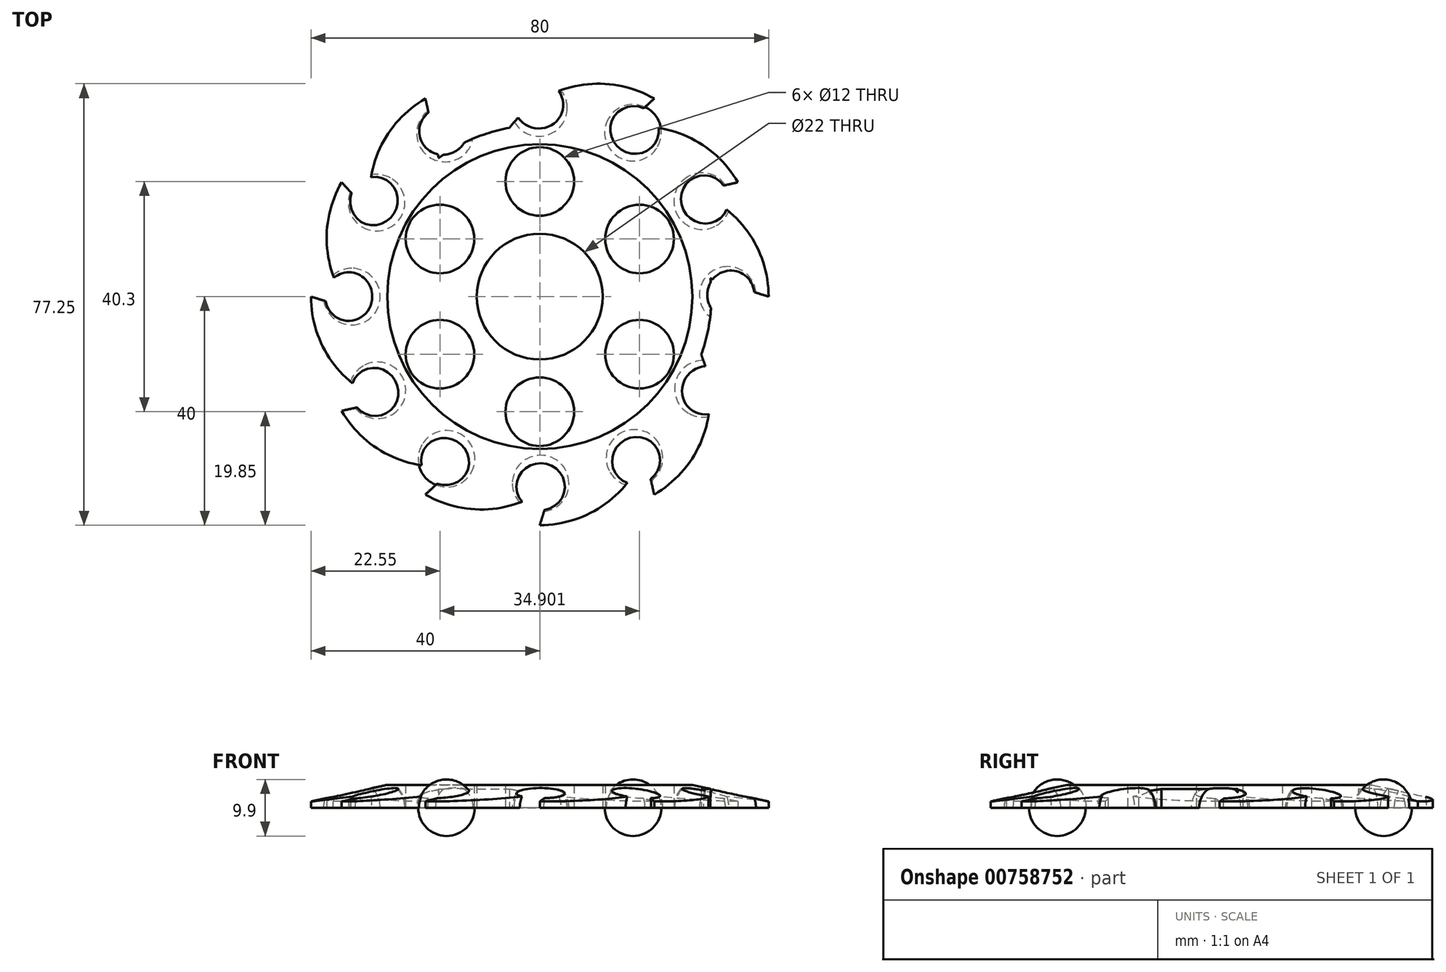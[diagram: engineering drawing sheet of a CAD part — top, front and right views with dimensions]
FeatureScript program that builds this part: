
annotation { "Feature Type Name" : "Feature", "Feature Type Description" : "" }
export const myFeature = defineFeature(function(context is Context, id is Id, definition is map)
    precondition{}
    {
        {
            assignVariable(context, id + "F0", {"name" : "thickness", "anyValue" : 8});
        }
        {
            var Q0;
            Q0=qCreatedBy(makeId("Top.planeOp"),FACE);
            var sketch = newSketch(context, id + "F1", { "sketchPlane" : qUnion([Q0])});
            skCircle(sketch, "E0", {"center": v(0, 0) * mm, "radius": 11 * mm});
            skCircle(sketch, "E1", {"center": v(0, 0) * mm, "radius": 40 * mm, "construction": true});
            skCircle(sketch, "E2", {"center": v(0, 0) * mm, "radius": 30 * mm});
            skLineSegment(sketch, "E3", {"start": v(-30, 0) * mm, "end": v(-11, 0) * mm, "construction": true});
            skPoint(sketch, "E4", {"position": v(-20.5, 0) * mm});
            skArc(sketch, "E5", {"start": v(-40, 0) * mm, "mid": v(-35.12, -12.9) * mm, "end": v(-22.93, -19.35) * mm});
            skArc(sketch, "E6.1.0", {"start": v(20, -34.64) * mm, "mid": v(28.73, -23.97) * mm, "end": v(28.22, -10.18) * mm});
            skArc(sketch, "E6.2.0", {"start": v(20, 34.64) * mm, "mid": v(6.39, 36.87) * mm, "end": v(-5.3, 29.53) * mm});
            skLineSegment(sketch, "E7", {"start": v(-40, 0) * mm, "end": v(-29.83, -3.17) * mm});
            skLineSegment(sketch, "E8.1.0", {"start": v(-34.64, -20) * mm, "end": v(-24.25, -17.66) * mm});
            skArc(sketch, "E8.1.1", {"start": v(-34.64, -20) * mm, "mid": v(-23.97, -28.73) * mm, "end": v(-10.18, -28.22) * mm});
            skLineSegment(sketch, "E8.2.0", {"start": v(-20, -34.64) * mm, "end": v(-12.17, -27.42) * mm});
            skArc(sketch, "E8.2.1", {"start": v(-20, -34.64) * mm, "mid": v(-6.39, -36.87) * mm, "end": v(5.3, -29.53) * mm});
            skLineSegment(sketch, "E9.1.3.0", {"start": v(0, -40) * mm, "end": v(3.17, -29.83) * mm});
            skArc(sketch, "E9.3.3.0", {"start": v(0, -40) * mm, "mid": v(12.9, -35.12) * mm, "end": v(19.35, -22.93) * mm});
            skLineSegment(sketch, "E9.1.4.0", {"start": v(20, -34.64) * mm, "end": v(17.66, -24.25) * mm});
            skLineSegment(sketch, "E9.1.5.0", {"start": v(34.64, -20) * mm, "end": v(27.42, -12.17) * mm});
            skArc(sketch, "E9.3.5.0", {"start": v(34.64, -20) * mm, "mid": v(36.87, -6.39) * mm, "end": v(29.53, 5.3) * mm});
            skLineSegment(sketch, "E10.1.6.0", {"start": v(40, 0) * mm, "end": v(29.83, 3.17) * mm});
            skArc(sketch, "E10.3.6.0", {"start": v(40, 0) * mm, "mid": v(35.12, 12.9) * mm, "end": v(22.93, 19.35) * mm});
            skLineSegment(sketch, "E10.1.7.0", {"start": v(34.64, 20) * mm, "end": v(24.25, 17.66) * mm});
            skArc(sketch, "E10.3.7.0", {"start": v(34.64, 20) * mm, "mid": v(23.97, 28.73) * mm, "end": v(10.18, 28.22) * mm});
            skLineSegment(sketch, "E11.1.8.0", {"start": v(20, 34.64) * mm, "end": v(12.17, 27.42) * mm});
            skLineSegment(sketch, "E11.1.9.0", {"start": v(0, 40) * mm, "end": v(-3.17, 29.83) * mm});
            skArc(sketch, "E11.3.9.0", {"start": v(0, 40) * mm, "mid": v(-12.9, 35.12) * mm, "end": v(-19.35, 22.93) * mm});
            skLineSegment(sketch, "E12.1.10.0", {"start": v(-20, 34.64) * mm, "end": v(-17.66, 24.25) * mm});
            skArc(sketch, "E12.3.10.0", {"start": v(-20, 34.64) * mm, "mid": v(-28.73, 23.97) * mm, "end": v(-28.22, 10.18) * mm});
            skLineSegment(sketch, "E12.1.11.0", {"start": v(-34.64, 20) * mm, "end": v(-27.42, 12.17) * mm});
            skArc(sketch, "E12.3.11.0", {"start": v(-34.64, 20) * mm, "mid": v(-36.87, 6.39) * mm, "end": v(-29.53, -5.3) * mm});
            skSolve(sketch);
        }
        {
            var Q0;
            {var subQ5=sQuery(id+"F1.wireOp",EDGE,"E8.2.1");var subQ7=sQuery(id+"F1.wireOp",EDGE,"E2");var subQ8=makeQuery(id+"F1.imprint","INTERSECT",VERTEX,{"derivedFrom":[subQ7,subQ5]});Q0=makeQuery(id+"F1.imprint","IMPRINT",FACE,{"disambiguationData":[TD([[makeQuery(id+"F1.imprint","IMPRINT",EDGE,{"disambiguationData":[TD([[subQ8,-1.0]])],"derivedFrom":subQ7}),-1.0]])]});}
            var Q1;
            {var subQ5=sQuery(id+"F1.wireOp",EDGE,"E9.3.3.0");var subQ7=sQuery(id+"F1.wireOp",EDGE,"E2");var subQ8=makeQuery(id+"F1.imprint","INTERSECT",VERTEX,{"derivedFrom":[subQ7,subQ5]});Q1=makeQuery(id+"F1.imprint","IMPRINT",FACE,{"disambiguationData":[TD([[makeQuery(id+"F1.imprint","IMPRINT",EDGE,{"disambiguationData":[TD([[subQ8,-1.0]])],"derivedFrom":subQ7}),-1.0]])]});}
            var Q2;
            {var subQ0=sQuery(id+"F1.wireOp",EDGE,"E8.2.1");var subQ1=sQuery(id+"F1.wireOp",EDGE,"E2");var subQ2=makeQuery(id+"F1.imprint","INTERSECT",VERTEX,{"derivedFrom":[subQ1,subQ0]});Q2=makeQuery(id+"F1.imprint","IMPRINT",FACE,{"disambiguationData":[TD([[makeQuery(id+"F1.imprint","IMPRINT",EDGE,{"disambiguationData":[TD([[subQ2,1.0]])],"derivedFrom":subQ1}),-1.0]])]});}
            var Q3;
            {var subQ3=sQuery(id+"F1.wireOp",EDGE,"E6.2.0");var subQ5=sQuery(id+"F1.wireOp",EDGE,"E2");var subQ6=makeQuery(id+"F1.imprint","INTERSECT",VERTEX,{"derivedFrom":[subQ5,subQ3]});Q3=makeQuery(id+"F1.imprint","IMPRINT",FACE,{"disambiguationData":[TD([[makeQuery(id+"F1.imprint","IMPRINT",EDGE,{"disambiguationData":[TD([[subQ6,-1.0]])],"derivedFrom":subQ5}),-1.0]])]});}
            var Q4;
            {var subQ5=sQuery(id+"F1.wireOp",EDGE,"E10.3.7.0");var subQ7=sQuery(id+"F1.wireOp",EDGE,"E2");var subQ8=makeQuery(id+"F1.imprint","INTERSECT",VERTEX,{"derivedFrom":[subQ7,subQ5]});Q4=makeQuery(id+"F1.imprint","IMPRINT",FACE,{"disambiguationData":[TD([[makeQuery(id+"F1.imprint","IMPRINT",EDGE,{"disambiguationData":[TD([[subQ8,-1.0]])],"derivedFrom":subQ7}),-1.0]])]});}
            var Q5;
            {var subQ5=sQuery(id+"F1.wireOp",EDGE,"E9.3.5.0");var subQ7=sQuery(id+"F1.wireOp",EDGE,"E2");var subQ8=makeQuery(id+"F1.imprint","INTERSECT",VERTEX,{"derivedFrom":[subQ7,subQ5]});Q5=makeQuery(id+"F1.imprint","IMPRINT",FACE,{"disambiguationData":[TD([[makeQuery(id+"F1.imprint","IMPRINT",EDGE,{"disambiguationData":[TD([[subQ8,-1.0]])],"derivedFrom":subQ7}),-1.0]])]});}
            var Q6;
            {var subQ0=sQuery(id+"F1.wireOp",EDGE,"E9.3.5.0");var subQ1=sQuery(id+"F1.wireOp",EDGE,"E2");var subQ2=makeQuery(id+"F1.imprint","INTERSECT",VERTEX,{"derivedFrom":[subQ1,subQ0]});Q6=makeQuery(id+"F1.imprint","IMPRINT",FACE,{"disambiguationData":[TD([[makeQuery(id+"F1.imprint","IMPRINT",EDGE,{"disambiguationData":[TD([[subQ2,1.0]])],"derivedFrom":subQ1}),-1.0]])]});}
            var Q7;
            {var subQ5=sQuery(id+"F1.wireOp",EDGE,"E8.1.1");var subQ6=sQuery(id+"F1.wireOp",EDGE,"E2");var subQ7=makeQuery(id+"F1.imprint","INTERSECT",VERTEX,{"derivedFrom":[subQ6,subQ5]});Q7=makeQuery(id+"F1.imprint","IMPRINT",FACE,{"disambiguationData":[TD([[makeQuery(id+"F1.imprint","IMPRINT",EDGE,{"disambiguationData":[TD([[subQ7,-1.0]])],"derivedFrom":subQ6}),-1.0]])]});}
            var Q8;
            {var subQ3=sQuery(id+"F1.wireOp",EDGE,"E5");var subQ7=sQuery(id+"F1.wireOp",EDGE,"E2");var subQ8=makeQuery(id+"F1.imprint","INTERSECT",VERTEX,{"derivedFrom":[subQ7,subQ3]});Q8=makeQuery(id+"F1.imprint","IMPRINT",FACE,{"disambiguationData":[TD([[makeQuery(id+"F1.imprint","IMPRINT",EDGE,{"disambiguationData":[TD([[subQ8,-1.0]])],"derivedFrom":subQ7}),-1.0]])]});}
            var Q9;
            {var subQ0=sQuery(id+"F1.wireOp",EDGE,"E10.3.6.0");var subQ1=sQuery(id+"F1.wireOp",EDGE,"E2");var subQ2=makeQuery(id+"F1.imprint","INTERSECT",VERTEX,{"derivedFrom":[subQ1,subQ0]});Q9=makeQuery(id+"F1.imprint","IMPRINT",FACE,{"disambiguationData":[TD([[makeQuery(id+"F1.imprint","IMPRINT",EDGE,{"disambiguationData":[TD([[subQ2,1.0]])],"derivedFrom":subQ1}),-1.0]])]});}
            var Q10;
            {var subQ5=sQuery(id+"F1.wireOp",EDGE,"E10.3.6.0");var subQ7=sQuery(id+"F1.wireOp",EDGE,"E2");var subQ8=makeQuery(id+"F1.imprint","INTERSECT",VERTEX,{"derivedFrom":[subQ7,subQ5]});Q10=makeQuery(id+"F1.imprint","IMPRINT",FACE,{"disambiguationData":[TD([[makeQuery(id+"F1.imprint","IMPRINT",EDGE,{"disambiguationData":[TD([[subQ8,-1.0]])],"derivedFrom":subQ7}),-1.0]])]});}
            var Q11;
            {var subQ5=sQuery(id+"F1.wireOp",EDGE,"E8.1.0");var subQ6=sQuery(id+"F1.wireOp",EDGE,"E2");var subQ7=makeQuery(id+"F1.imprint","INTERSECT",VERTEX,{"derivedFrom":[subQ6,subQ5]});Q11=makeQuery(id+"F1.imprint","IMPRINT",FACE,{"disambiguationData":[TD([[makeQuery(id+"F1.imprint","IMPRINT",EDGE,{"disambiguationData":[TD([[subQ7,1.0]])],"derivedFrom":subQ6}),-1.0]])]});}
            var Q12;
            {var subQ5=sQuery(id+"F1.wireOp",EDGE,"E6.1.0");var subQ7=sQuery(id+"F1.wireOp",EDGE,"E2");var subQ8=makeQuery(id+"F1.imprint","INTERSECT",VERTEX,{"derivedFrom":[subQ7,subQ5]});Q12=makeQuery(id+"F1.imprint","IMPRINT",FACE,{"disambiguationData":[TD([[makeQuery(id+"F1.imprint","IMPRINT",EDGE,{"disambiguationData":[TD([[subQ8,-1.0]])],"derivedFrom":subQ7}),-1.0]])]});}
            var Q13;
            {var subQ5=sQuery(id+"F1.wireOp",EDGE,"E11.3.9.0");var subQ6=sQuery(id+"F1.wireOp",EDGE,"E2");var subQ7=makeQuery(id+"F1.imprint","INTERSECT",VERTEX,{"derivedFrom":[subQ6,subQ5]});Q13=makeQuery(id+"F1.imprint","IMPRINT",FACE,{"disambiguationData":[TD([[makeQuery(id+"F1.imprint","IMPRINT",EDGE,{"disambiguationData":[TD([[subQ7,-1.0]])],"derivedFrom":subQ6}),-1.0]])]});}
            var Q14;
            {var subQ5=sQuery(id+"F1.wireOp",EDGE,"E2");var subQ7=sQuery(id+"F1.wireOp",EDGE,"E7");var subQ8=makeQuery(id+"F1.imprint","INTERSECT",VERTEX,{"derivedFrom":[subQ5,subQ7]});Q14=makeQuery(id+"F1.imprint","IMPRINT",FACE,{"disambiguationData":[TD([[makeQuery(id+"F1.imprint","IMPRINT",EDGE,{"disambiguationData":[TD([[subQ8,1.0]])],"derivedFrom":subQ5}),-1.0]])]});}
            var Q15;
            Q15=makeQuery(id+"F1.imprint","IMPRINT",FACE,{"disambiguationData":[TD([[makeQuery(id+"F1.imprint","IMPRINT",EDGE,{"derivedFrom":sQuery(id+"F1.wireOp",EDGE,"E0")}),-1.0]])]});
            var Q16;
            {var subQ0=sQuery(id+"F1.wireOp",EDGE,"E8.1.1");var subQ1=sQuery(id+"F1.wireOp",EDGE,"E2");var subQ2=makeQuery(id+"F1.imprint","INTERSECT",VERTEX,{"derivedFrom":[subQ1,subQ0]});Q16=makeQuery(id+"F1.imprint","IMPRINT",FACE,{"disambiguationData":[TD([[makeQuery(id+"F1.imprint","IMPRINT",EDGE,{"disambiguationData":[TD([[subQ2,1.0]])],"derivedFrom":subQ1}),-1.0]])]});}
            var Q17;
            {var subQ0=sQuery(id+"F1.wireOp",EDGE,"E9.3.3.0");var subQ1=sQuery(id+"F1.wireOp",EDGE,"E2");var subQ2=makeQuery(id+"F1.imprint","INTERSECT",VERTEX,{"derivedFrom":[subQ1,subQ0]});Q17=makeQuery(id+"F1.imprint","IMPRINT",FACE,{"disambiguationData":[TD([[makeQuery(id+"F1.imprint","IMPRINT",EDGE,{"disambiguationData":[TD([[subQ2,1.0]])],"derivedFrom":subQ1}),-1.0]])]});}
            var Q18;
            {var subQ0=sQuery(id+"F1.wireOp",EDGE,"E11.3.9.0");var subQ1=sQuery(id+"F1.wireOp",EDGE,"E2");var subQ2=makeQuery(id+"F1.imprint","INTERSECT",VERTEX,{"derivedFrom":[subQ1,subQ0]});Q18=makeQuery(id+"F1.imprint","IMPRINT",FACE,{"disambiguationData":[TD([[makeQuery(id+"F1.imprint","IMPRINT",EDGE,{"disambiguationData":[TD([[subQ2,1.0]])],"derivedFrom":subQ1}),-1.0]])]});}
            var Q19;
            {var subQ0=sQuery(id+"F1.wireOp",EDGE,"E10.3.7.0");var subQ1=sQuery(id+"F1.wireOp",EDGE,"E2");var subQ2=makeQuery(id+"F1.imprint","INTERSECT",VERTEX,{"derivedFrom":[subQ1,subQ0]});Q19=makeQuery(id+"F1.imprint","IMPRINT",FACE,{"disambiguationData":[TD([[makeQuery(id+"F1.imprint","IMPRINT",EDGE,{"disambiguationData":[TD([[subQ2,1.0]])],"derivedFrom":subQ1}),-1.0]])]});}
            var Q20;
            {var subQ0=sQuery(id+"F1.wireOp",EDGE,"E6.2.0");var subQ1=sQuery(id+"F1.wireOp",EDGE,"E2");var subQ2=makeQuery(id+"F1.imprint","INTERSECT",VERTEX,{"derivedFrom":[subQ1,subQ0]});Q20=makeQuery(id+"F1.imprint","IMPRINT",FACE,{"disambiguationData":[TD([[makeQuery(id+"F1.imprint","IMPRINT",EDGE,{"disambiguationData":[TD([[subQ2,1.0]])],"derivedFrom":subQ1}),-1.0]])]});}
            var Q21;
            {var subQ0=sQuery(id+"F1.wireOp",EDGE,"E7");var subQ1=sQuery(id+"F1.wireOp",EDGE,"E2");var subQ2=makeQuery(id+"F1.imprint","INTERSECT",VERTEX,{"derivedFrom":[subQ1,subQ0]});Q21=makeQuery(id+"F1.imprint","IMPRINT",FACE,{"disambiguationData":[TD([[makeQuery(id+"F1.imprint","IMPRINT",EDGE,{"disambiguationData":[TD([[subQ2,-1.0]])],"derivedFrom":subQ1}),-1.0]])]});}
            var Q22;
            {var subQ0=sQuery(id+"F1.wireOp",EDGE,"E5");var subQ1=sQuery(id+"F1.wireOp",EDGE,"E2");var subQ2=makeQuery(id+"F1.imprint","INTERSECT",VERTEX,{"derivedFrom":[subQ1,subQ0]});Q22=makeQuery(id+"F1.imprint","IMPRINT",FACE,{"disambiguationData":[TD([[makeQuery(id+"F1.imprint","IMPRINT",EDGE,{"disambiguationData":[TD([[subQ2,1.0]])],"derivedFrom":subQ1}),-1.0]])]});}
            var Q23;
            {var subQ0=sQuery(id+"F1.wireOp",EDGE,"E12.3.10.0");var subQ1=sQuery(id+"F1.wireOp",EDGE,"E2");var subQ2=makeQuery(id+"F1.imprint","INTERSECT",VERTEX,{"derivedFrom":[subQ1,subQ0]});Q23=makeQuery(id+"F1.imprint","IMPRINT",FACE,{"disambiguationData":[TD([[makeQuery(id+"F1.imprint","IMPRINT",EDGE,{"disambiguationData":[TD([[subQ2,1.0]])],"derivedFrom":subQ1}),-1.0]])]});}
            var Q24;
            {var subQ0=sQuery(id+"F1.wireOp",EDGE,"E6.1.0");var subQ1=sQuery(id+"F1.wireOp",EDGE,"E2");var subQ2=makeQuery(id+"F1.imprint","INTERSECT",VERTEX,{"derivedFrom":[subQ1,subQ0]});Q24=makeQuery(id+"F1.imprint","IMPRINT",FACE,{"disambiguationData":[TD([[makeQuery(id+"F1.imprint","IMPRINT",EDGE,{"disambiguationData":[TD([[subQ2,1.0]])],"derivedFrom":subQ1}),-1.0]])]});}
            extrude(context, id + "F2", {"entities" : qUnion([Q0, Q1, Q2, Q3, Q4, Q5, Q6, Q7, Q8, Q9, Q10, Q11, Q12, Q13, Q14, Q15, Q16, Q17, Q18, Q19, Q20, Q21, Q22, Q23, Q24]), "depth" : (getVariable(context, 'thickness') / 2) * mm, "offsetDistance" : 25 * mm});
        }
        {
            var Q0;
            Q0=qCreatedBy(makeId("Top.planeOp"),FACE);
            var sketch = newSketch(context, id + "F3", { "sketchPlane" : qUnion([Q0])});
            skArc(sketch, "E13", {"start": v(-32.86, 4.95) * mm, "mid": v(-37.8, 0) * mm, "end": v(-32.86, -4.95) * mm});
            skLineSegment(sketch, "E14", {"start": v(-32.86, 4.95) * mm, "end": v(-32.86, -4.95) * mm});
            skLineSegment(sketch, "E15", {"start": v(0, 5.47) * mm, "end": v(0, -6.23) * mm, "construction": true});
            skArc(sketch, "E16.1.0", {"start": v(-30.86, -12.12) * mm, "mid": v(-32.67, -18.88) * mm, "end": v(-25.9, -20.7) * mm});
            skLineSegment(sketch, "E16.1.1", {"start": v(-30.86, -12.12) * mm, "end": v(-25.9, -20.7) * mm});
            skArc(sketch, "E16.2.0", {"start": v(-20.59, -25.9) * mm, "mid": v(-18.77, -32.67) * mm, "end": v(-12.01, -30.86) * mm});
            skLineSegment(sketch, "E16.2.1", {"start": v(-20.59, -25.9) * mm, "end": v(-12.01, -30.86) * mm});
            skArc(sketch, "E16.3.0", {"start": v(-4.8, -32.7) * mm, "mid": v(0.15, -37.66) * mm, "end": v(5.1, -32.7) * mm});
            skLineSegment(sketch, "E16.3.1", {"start": v(-4.8, -32.7) * mm, "end": v(5.1, -32.7) * mm});
            skArc(sketch, "E16.4.0", {"start": v(12.27, -30.7) * mm, "mid": v(19.03, -32.52) * mm, "end": v(20.85, -25.76) * mm});
            skLineSegment(sketch, "E16.4.1", {"start": v(12.27, -30.7) * mm, "end": v(20.85, -25.76) * mm});
            skArc(sketch, "E16.5.0", {"start": v(26.06, -20.44) * mm, "mid": v(32.82, -18.62) * mm, "end": v(31, -11.86) * mm});
            skLineSegment(sketch, "E16.5.1", {"start": v(26.06, -20.44) * mm, "end": v(31, -11.86) * mm});
            skArc(sketch, "E16.6.0", {"start": v(32.86, -4.65) * mm, "mid": v(37.8, 0.3) * mm, "end": v(32.86, 5.25) * mm});
            skLineSegment(sketch, "E16.6.1", {"start": v(32.86, -4.65) * mm, "end": v(32.86, 5.25) * mm});
            skArc(sketch, "E16.7.0", {"start": v(30.86, 12.42) * mm, "mid": v(32.67, 19.18) * mm, "end": v(25.9, 21) * mm});
            skLineSegment(sketch, "E16.7.1", {"start": v(30.86, 12.42) * mm, "end": v(25.9, 21) * mm});
            skArc(sketch, "E16.8.0", {"start": v(20.59, 26.2) * mm, "mid": v(18.77, 32.97) * mm, "end": v(12.01, 31.16) * mm});
            skLineSegment(sketch, "E16.8.1", {"start": v(20.59, 26.2) * mm, "end": v(12.01, 31.16) * mm});
            skArc(sketch, "E16.9.0", {"start": v(4.8, 33) * mm, "mid": v(-0.15, 37.96) * mm, "end": v(-5.1, 33) * mm});
            skLineSegment(sketch, "E16.9.1", {"start": v(4.8, 33) * mm, "end": v(-5.1, 33) * mm});
            skArc(sketch, "E16.10.0", {"start": v(-12.27, 31) * mm, "mid": v(-19.03, 32.82) * mm, "end": v(-20.85, 26.06) * mm});
            skLineSegment(sketch, "E16.10.1", {"start": v(-12.27, 31) * mm, "end": v(-20.85, 26.06) * mm});
            skArc(sketch, "E16.11.0", {"start": v(-26.06, 20.74) * mm, "mid": v(-32.82, 18.92) * mm, "end": v(-31, 12.16) * mm});
            skLineSegment(sketch, "E16.11.1", {"start": v(-26.06, 20.74) * mm, "end": v(-31, 12.16) * mm});
            skPoint(sketch, "E16.center", {"position": v(0, 0.15) * mm});
            skSolve(sketch);
        }
        {
            var Q0;
            Q0=makeQuery(id+"F3.imprint","IMPRINT",FACE,{"disambiguationData":[TD([[makeQuery(id+"F3.imprint","IMPRINT",EDGE,{"derivedFrom":sQuery(id+"F3.wireOp",EDGE,"E13")}),1.0]])]});
            var Q1;
            Q1=sQuery(id+"F3.wireOp",EDGE,"E14");
            revolve(context, id + "F4", {"operationType" : NewBodyOperationType.REMOVE, "surfaceOperationType" : NewSurfaceOperationType.NEW, "entities" : qUnion([Q0]), "axis" : qUnion([Q1]), "revolveType" : RevolveType.FULL});
        }
        {
            var Q0;
            Q0=makeQuery(id+"F3.imprint","IMPRINT",FACE,{"disambiguationData":[TD([[makeQuery(id+"F3.imprint","IMPRINT",EDGE,{"derivedFrom":sQuery(id+"F3.wireOp",EDGE,"E16.1.0")}),1.0]])]});
            var Q1;
            Q1=sQuery(id+"F3.wireOp",EDGE,"E16.1.1");
            revolve(context, id + "F5", {"operationType" : NewBodyOperationType.REMOVE, "surfaceOperationType" : NewSurfaceOperationType.NEW, "entities" : qUnion([Q0]), "axis" : qUnion([Q1]), "revolveType" : RevolveType.FULL, "oppositeDirection" : true});
        }
        {
            var Q0;
            Q0=makeQuery(id+"F3.imprint","IMPRINT",FACE,{"disambiguationData":[TD([[makeQuery(id+"F3.imprint","IMPRINT",EDGE,{"derivedFrom":sQuery(id+"F3.wireOp",EDGE,"E16.2.0")}),1.0]])]});
            var Q1;
            Q1=sQuery(id+"F3.wireOp",EDGE,"E16.2.1");
            revolve(context, id + "F6", {"operationType" : NewBodyOperationType.REMOVE, "surfaceOperationType" : NewSurfaceOperationType.NEW, "entities" : qUnion([Q0]), "axis" : qUnion([Q1]), "revolveType" : RevolveType.FULL, "oppositeDirection" : true});
        }
        {
            var Q0;
            Q0=makeQuery(id+"F3.imprint","IMPRINT",FACE,{"disambiguationData":[TD([[makeQuery(id+"F3.imprint","IMPRINT",EDGE,{"derivedFrom":sQuery(id+"F3.wireOp",EDGE,"E16.3.0")}),1.0]])]});
            var Q1;
            Q1=sQuery(id+"F3.wireOp",EDGE,"E16.3.1");
            revolve(context, id + "F7", {"operationType" : NewBodyOperationType.REMOVE, "surfaceOperationType" : NewSurfaceOperationType.NEW, "entities" : qUnion([Q0]), "axis" : qUnion([Q1]), "revolveType" : RevolveType.FULL});
        }
        {
            var Q0;
            Q0=makeQuery(id+"F3.imprint","IMPRINT",FACE,{"disambiguationData":[TD([[makeQuery(id+"F3.imprint","IMPRINT",EDGE,{"derivedFrom":sQuery(id+"F3.wireOp",EDGE,"E16.4.0")}),1.0]])]});
            var Q1;
            Q1=sQuery(id+"F3.wireOp",EDGE,"E16.4.1");
            revolve(context, id + "F8", {"operationType" : NewBodyOperationType.REMOVE, "surfaceOperationType" : NewSurfaceOperationType.NEW, "entities" : qUnion([Q0]), "axis" : qUnion([Q1]), "revolveType" : RevolveType.FULL, "oppositeDirection" : true});
        }
        {
            var Q0;
            Q0=makeQuery(id+"F3.imprint","IMPRINT",FACE,{"disambiguationData":[TD([[makeQuery(id+"F3.imprint","IMPRINT",EDGE,{"derivedFrom":sQuery(id+"F3.wireOp",EDGE,"E16.5.0")}),1.0]])]});
            var Q1;
            Q1=sQuery(id+"F3.wireOp",EDGE,"E16.5.1");
            revolve(context, id + "F9", {"operationType" : NewBodyOperationType.REMOVE, "surfaceOperationType" : NewSurfaceOperationType.NEW, "entities" : qUnion([Q0]), "axis" : qUnion([Q1]), "revolveType" : RevolveType.FULL});
        }
        {
            var Q0;
            Q0=makeQuery(id+"F3.imprint","IMPRINT",FACE,{"disambiguationData":[TD([[makeQuery(id+"F3.imprint","IMPRINT",EDGE,{"derivedFrom":sQuery(id+"F3.wireOp",EDGE,"E16.6.0")}),1.0]])]});
            var Q1;
            Q1=sQuery(id+"F3.wireOp",EDGE,"E16.6.1");
            revolve(context, id + "F10", {"operationType" : NewBodyOperationType.REMOVE, "surfaceOperationType" : NewSurfaceOperationType.NEW, "entities" : qUnion([Q0]), "axis" : qUnion([Q1]), "revolveType" : RevolveType.FULL, "oppositeDirection" : true});
        }
        {
            var Q0;
            Q0=makeQuery(id+"F3.imprint","IMPRINT",FACE,{"disambiguationData":[TD([[makeQuery(id+"F3.imprint","IMPRINT",EDGE,{"derivedFrom":sQuery(id+"F3.wireOp",EDGE,"E16.7.0")}),1.0]])]});
            var Q1;
            Q1=sQuery(id+"F3.wireOp",EDGE,"E16.7.1");
            revolve(context, id + "F11", {"operationType" : NewBodyOperationType.REMOVE, "surfaceOperationType" : NewSurfaceOperationType.NEW, "entities" : qUnion([Q0]), "axis" : qUnion([Q1]), "revolveType" : RevolveType.FULL, "oppositeDirection" : true});
        }
        {
            var Q0;
            Q0=makeQuery(id+"F3.imprint","IMPRINT",FACE,{"disambiguationData":[TD([[makeQuery(id+"F3.imprint","IMPRINT",EDGE,{"derivedFrom":sQuery(id+"F3.wireOp",EDGE,"E16.11.0")}),1.0]])]});
            var Q1;
            Q1=sQuery(id+"F3.wireOp",EDGE,"E16.11.1");
            revolve(context, id + "F12", {"operationType" : NewBodyOperationType.REMOVE, "surfaceOperationType" : NewSurfaceOperationType.NEW, "entities" : qUnion([Q0]), "axis" : qUnion([Q1]), "revolveType" : RevolveType.FULL, "oppositeDirection" : true});
        }
        {
            var Q0;
            Q0=makeQuery(id+"F3.imprint","IMPRINT",FACE,{"disambiguationData":[TD([[makeQuery(id+"F3.imprint","IMPRINT",EDGE,{"derivedFrom":sQuery(id+"F3.wireOp",EDGE,"E16.10.0")}),1.0]])]});
            var Q1;
            Q1=sQuery(id+"F3.wireOp",EDGE,"E16.10.1");
            revolve(context, id + "F13", {"operationType" : NewBodyOperationType.REMOVE, "surfaceOperationType" : NewSurfaceOperationType.NEW, "entities" : qUnion([Q0]), "axis" : qUnion([Q1]), "revolveType" : RevolveType.FULL, "oppositeDirection" : true});
        }
        {
            var Q0;
            Q0=makeQuery(id+"F3.imprint","IMPRINT",FACE,{"disambiguationData":[TD([[makeQuery(id+"F3.imprint","IMPRINT",EDGE,{"derivedFrom":sQuery(id+"F3.wireOp",EDGE,"E16.9.0")}),1.0]])]});
            var Q1;
            Q1=sQuery(id+"F3.wireOp",EDGE,"E16.9.1");
            revolve(context, id + "F14", {"operationType" : NewBodyOperationType.REMOVE, "surfaceOperationType" : NewSurfaceOperationType.NEW, "entities" : qUnion([Q0]), "axis" : qUnion([Q1]), "revolveType" : RevolveType.FULL, "oppositeDirection" : true});
        }
        {
            var Q0;
            Q0=makeQuery(id+"F3.imprint","IMPRINT",FACE,{"disambiguationData":[TD([[makeQuery(id+"F3.imprint","IMPRINT",EDGE,{"derivedFrom":sQuery(id+"F3.wireOp",EDGE,"E16.8.0")}),1.0]])]});
            var Q1;
            Q1=sQuery(id+"F3.wireOp",EDGE,"E16.8.1");
            revolve(context, id + "F15", {"operationType" : NewBodyOperationType.REMOVE, "surfaceOperationType" : NewSurfaceOperationType.NEW, "entities" : qUnion([Q0]), "axis" : qUnion([Q1]), "revolveType" : RevolveType.FULL, "oppositeDirection" : true});
        }
        {
            var Q0;
            Q0=qCreatedBy(makeId("Front.planeOp"),FACE);
            var sketch = newSketch(context, id + "F16", { "sketchPlane" : qUnion([Q0])});
            skLineSegment(sketch, "E17", {"start": v(-45, 0) * mm, "end": v(-26.67, 4) * mm});
            skLineSegment(sketch, "E18", {"start": v(-26.67, 4) * mm, "end": v(-51.76, 4) * mm});
            skLineSegment(sketch, "E19", {"start": v(-51.76, 4) * mm, "end": v(-51.76, 0) * mm});
            skLineSegment(sketch, "E20", {"start": v(-51.76, 0) * mm, "end": v(-45, 0) * mm});
            skLineSegment(sketch, "E21", {"start": v(0, 10.58) * mm, "end": v(0, -13) * mm, "construction": true});
            skLineSegment(sketch, "E22.MirrorCS", {"start": v(-51.76, -4) * mm, "end": v(-51.76, 0) * mm});
            skLineSegment(sketch, "E23.MirrorCS", {"start": v(-26.67, -4) * mm, "end": v(-51.76, -4) * mm});
            skLineSegment(sketch, "E24.MirrorCS", {"start": v(-45, 0) * mm, "end": v(-26.67, -4) * mm});
            skSolve(sketch);
        }
        {
            var Q0;
            Q0=makeQuery(id+"F16.imprint","IMPRINT",FACE,{"disambiguationData":[TD([[makeQuery(id+"F16.imprint","IMPRINT",EDGE,{"derivedFrom":sQuery(id+"F16.wireOp",EDGE,"E17")}),1.0]])]});
            var Q1;
            Q1=makeQuery(id+"F16.imprint","IMPRINT",FACE,{"disambiguationData":[TD([[makeQuery(id+"F16.imprint","IMPRINT",EDGE,{"derivedFrom":sQuery(id+"F16.wireOp",EDGE,"E20")}),-1.0]])]});
            var Q2;
            Q2=sQuery(id+"F16.wireOp",EDGE,"E21");
            revolve(context, id + "F17", {"operationType" : NewBodyOperationType.REMOVE, "surfaceOperationType" : NewSurfaceOperationType.NEW, "entities" : qUnion([Q0, Q1]), "axis" : qUnion([Q2]), "revolveType" : RevolveType.FULL, "oppositeDirection" : true});
        }
        {
            var Q0;
            Q0=makeQuery(id+"F2.opExtrude","CAP_FACE",FACE,{"disambiguationData":[OSD([sQuery(id+"F1.wireOp",EDGE,"E0"),sQuery(id+"F1.wireOp",EDGE,"E5"),sQuery(id+"F1.wireOp",EDGE,"E7"),sQuery(id+"F1.wireOp",EDGE,"E8.1.0"),sQuery(id+"F1.wireOp",EDGE,"E8.1.1"),sQuery(id+"F1.wireOp",EDGE,"E8.2.0"),sQuery(id+"F1.wireOp",EDGE,"E8.2.1"),sQuery(id+"F1.wireOp",EDGE,"E9.1.3.0"),sQuery(id+"F1.wireOp",EDGE,"E9.3.3.0"),sQuery(id+"F1.wireOp",EDGE,"E9.1.4.0"),sQuery(id+"F1.wireOp",EDGE,"E6.1.0"),sQuery(id+"F1.wireOp",EDGE,"E9.1.5.0"),sQuery(id+"F1.wireOp",EDGE,"E9.3.5.0"),sQuery(id+"F1.wireOp",EDGE,"E10.1.6.0"),sQuery(id+"F1.wireOp",EDGE,"E10.3.6.0"),sQuery(id+"F1.wireOp",EDGE,"E10.1.7.0"),sQuery(id+"F1.wireOp",EDGE,"E10.3.7.0"),sQuery(id+"F1.wireOp",EDGE,"E11.1.8.0"),sQuery(id+"F1.wireOp",EDGE,"E6.2.0"),sQuery(id+"F1.wireOp",EDGE,"E11.1.9.0"),sQuery(id+"F1.wireOp",EDGE,"E11.3.9.0"),sQuery(id+"F1.wireOp",EDGE,"E12.1.10.0"),sQuery(id+"F1.wireOp",EDGE,"E12.3.10.0"),sQuery(id+"F1.wireOp",EDGE,"E12.1.11.0"),sQuery(id+"F1.wireOp",EDGE,"E12.3.11.0")])],"isStart":false});
            var sketch = newSketch(context, id + "F18", { "sketchPlane" : qUnion([Q0])});
            skCircle(sketch, "E25", {"center": v(0, 20.15) * mm, "radius": 6 * mm});
            skCircle(sketch, "E26.1.0", {"center": v(-17.45, 10.08) * mm, "radius": 6 * mm});
            skCircle(sketch, "E26.2.0", {"center": v(-17.45, -10.07) * mm, "radius": 6 * mm});
            skCircle(sketch, "E26.3.0", {"center": v(0, -20.15) * mm, "radius": 6 * mm});
            skCircle(sketch, "E26.4.0", {"center": v(17.45, -10.08) * mm, "radius": 6 * mm});
            skCircle(sketch, "E26.5.0", {"center": v(17.45, 10.07) * mm, "radius": 6 * mm});
            skPoint(sketch, "E26.center", {"position": v(0, 0) * mm});
            skSolve(sketch);
        }
        {
            var Q0;
            Q0=qSketchRegion(id+"F18",true);
            extrude(context, id + "F19", {"entities" : qUnion([Q0]), "operationType" : NewBodyOperationType.REMOVE, "endBound" : BoundingType.SYMMETRIC, "depth" : 25 * mm, "offsetDistance" : 25 * mm});
        }
    });
